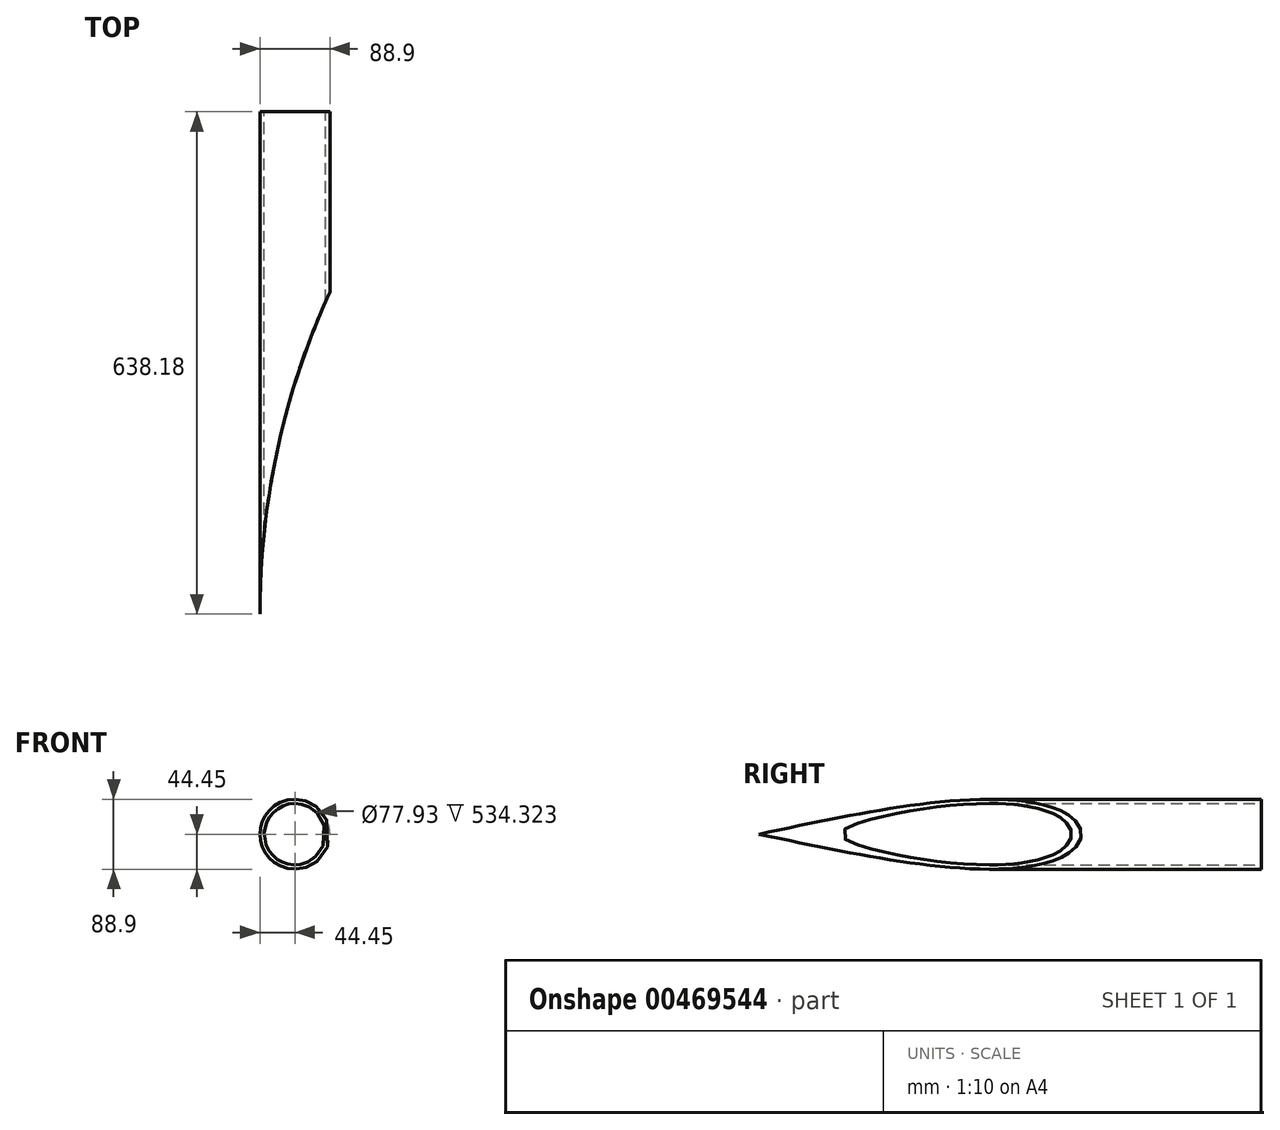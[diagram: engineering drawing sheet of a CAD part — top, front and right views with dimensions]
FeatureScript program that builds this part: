
annotation { "Feature Type Name" : "Feature", "Feature Type Description" : "" }
export const myFeature = defineFeature(function(context is Context, id is Id, definition is map)
    precondition{}
    {
        {
            var Q0;
            Q0=qCreatedBy(makeId("Front.planeOp"),FACE);
            var sketch = newSketch(context, id + "F0", { "sketchPlane" : qUnion([Q0])});
            skCircle(sketch, "E0", {"center": v(0, 0) * mm, "radius": 44.45 * mm});
            skCircle(sketch, "E1", {"center": v(0, 0) * mm, "radius": 38.96 * mm});
            skSolve(sketch);
        }
        {
            var Q0;
            Q0 = qSketchRegion(id + "F0", true);
            extrude(context, id + "F1", {"entities" : qUnion([Q0]), "depth" : 638.17 * mm, "offsetDistance" : 25.4 * mm});
        }
        {
            var Q0;
            Q0=qCreatedBy(makeId("Top.planeOp"),FACE);
            var sketch = newSketch(context, id + "F2", { "sketchPlane" : qUnion([Q0])});
            skCircle(sketch, "E2", {"center": v(943.1, -638.18) * mm, "radius": 987.55 * mm});
            skSolve(sketch);
        }
        {
            var Q0;
            Q0 = qSketchRegion(id + "F2", true);
            extrude(context, id + "F3", {"entities" : qUnion([Q0]), "operationType" : NewBodyOperationType.REMOVE, "endBound" : BoundingType.THROUGH_ALL, "oppositeDirection" : true, "depth" : 25.4 * mm, "offsetDistance" : 25.4 * mm, "hasSecondDirection" : true, "secondDirectionBound" : SecondDirectionBoundingType.THROUGH_ALL, "secondDirectionOppositeDirection" : false, "secondDirectionDepth" : 25.4 * mm});
        }
    });
